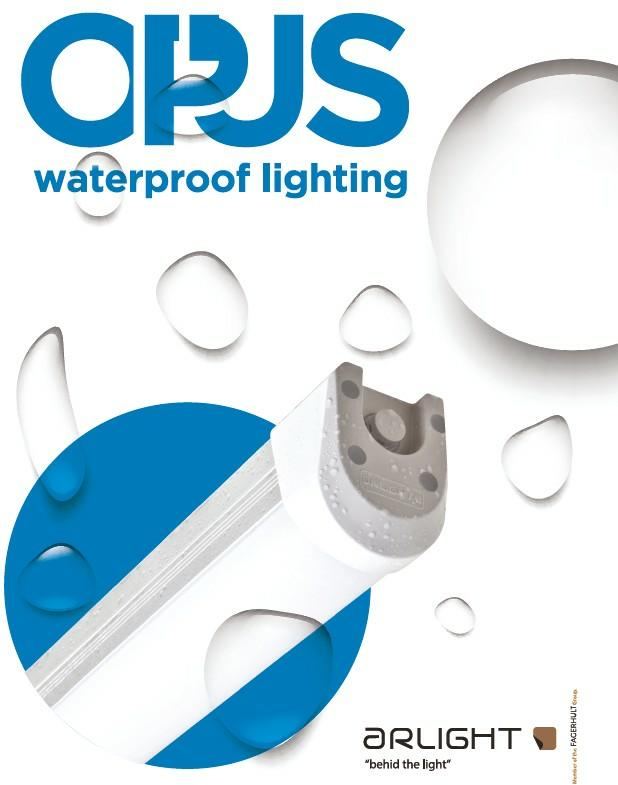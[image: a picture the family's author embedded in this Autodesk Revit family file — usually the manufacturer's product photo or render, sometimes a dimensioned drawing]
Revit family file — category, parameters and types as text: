
# Revit family: E 1500 PUS
name_source: partatom
category: Lighting Fixtures
revit_build: Autodesk Revit 2017 (Build: 20160225_1515(x64)
units: mm (PartAtom-declared; Revit-internal decimal feet)

## family parameters
Cut with Voids When Loaded = No
Host = Face
Light Source = Yes
Part Type = Normal
Room Calculation Point = No
Round Connector Dimension = Use Diameter
Shared = No

## types (8) — shared parameters
Color Filter = 16777215
Default Elevation = 1219 mm
Description = Double Connector
Dimming Lamp Color Temperature Shift = <None>
Emit Shape Visible in Rendering = No
Emit from Rectangle Length = 1427 mm  [stored 4.68176 ft]
Emit from Rectangle Width = 55 mm  [stored 0.180446 ft]
Lamp = LED
Manufacturer = ARLIGHT AYDINLATMA
Model = E 1500 PUS (CK)
Photometric Web File = E 1500 PUS-59W-4K(SK).IES
Tilt Angle = -90.00°
Type Comments = Waterproof Lighting
Type Image = OPUS.jpg
URL = http://www.arlight.net

## per-type parameters (varying)
| type | Apparent Load | Wattage Comments |
| EPUS.1500.44.40.TK | 44 VA | 44W |
| EPUS.1500.61.40.TK | 61 VA | 61W |
| EPUS.1500.44.40.CK | 44 VA | 44W |
| EPUS.1500.61.40.CK | 61 VA | 61W |
| EPUS.1500.44.40.TR | 44 VA | 44W |
| EPUS.1500.61.40.TR | 61 VA | 61W |
| EPUS.1500.44.40.CR | 44 VA | 44W |
| EPUS.1500.61.40.CR | 61 VA | 61W |

note: [stored X ft] marks values corroborated as IEEE doubles in the binary element streams (Revit-internal decimal feet)

## geometry (parser evidence)
native form markers: Sweep x3
no freeform markers — native parametric forms only
